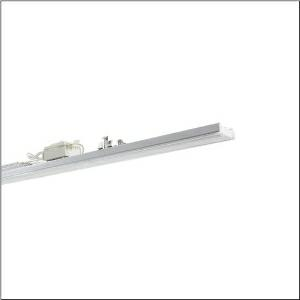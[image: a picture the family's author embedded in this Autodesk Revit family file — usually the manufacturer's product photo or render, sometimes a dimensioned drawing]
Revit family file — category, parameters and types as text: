
# Revit family: licross_r__11_recessed_ho_51tl18dv4m1m_dde3
name_source: partatom
category: Lighting Fixtures
units: mm (PartAtom-declared; Revit-internal decimal feet)

## family parameters
Cut with Voids When Loaded = No
Host = Face
Light Source = No
Part Type = Normal
Room Calculation Point = No
Round Connector Dimension = Use Diameter
Shared = No

## types (1)
- --- (1 x LED, 26860 lm, 150.5 W, 4000K)
    Apparent Load = 150 VA
    CIE Flux Codes = 78 94 99 100 100
    Color Rendering = 80
    Color Temperature = 4000K
    Default Elevation = 1800 mm
    Description = Licross® 11 Recessed HO, luminaire insert, of sheet steel, coil coated, white, length: 2.250mm, width: 66mm, height: 67mm, LED rated luminous flux: 26.870lm, light colour: 840, control gear: DALI 2, with plug, 5-pole, with phase selection, mains connection: 220..240V, AC, 50/60Hz, rated input power: 151W, halogen-free wiring, primary light control with lens, of plastic, primary optical cover: cover, of PMMA, light emission: direct distribution, primary light characteristic: symmetric, protection rating (complete): IP40, insulation class (complete): insulation class I (protective earthing), certification: CE, ENEC, VDE, UKCA, protection symbol: D if used in an environment without relevant dust loads with corresponding accessories, impact resistance: IK06, permissible ambient temperature for indoor applications: -40..+35°C, corresponds to IFS (International Featured Standards) requirements for safety and quality in the food industry, reducing of maximum allowable ambient temperature of 5°C with ceiling mounting, LABS conformity tested according to VDMA 24364:2018-05, packaging unit: 1 piece
    Height = 58 mm
    Lamp = 1 x LED
    Lamp Light Flux = 26860 lm
    Lamp Power = 150.5 W
    Lamp count = 1
    Length = 2250 mm
    Luminous efficacy = 178 lm/W
    Manufacturer = Siteco
    ModVariant = No
    Model = 51TL18DV4M1M
    Mounting Place = Ceiling
    Mounting Type = Pendant
    Number of Poles = 1
    OnlyDefault = Yes
    Power Factor = 1
    Product Name = Licross® 11 Recessed HO
    Product group = luminaire insert
    ProductGroupID = 902
    Protection Class = Protection class I
    Protection Degree = IP 40
    RLX_Detail_Level = 1
    RLX_Emergency_Light_Flux = 0 lm
    RLX_Emergency_Type = 0
    RLX_Emergency_Type_DB = No
    RlxData = <blob elided: 29361 chars, md5=500fe299>
    Socket = socket
    Standby Power = 0 W
    System Light Flux = 26860 lm
    System Power = 150 W
    Type Comments = factory setting: luminous flux: 100 % | dim-lin: 254 | 690 mA
    Type Image = l_1296930.jpg
    URL = http://relux.com
    VarID = @adj_099446
    Voltage = 0 V
    Weight = 0.00 kg
    Width = 66 mm

## geometry (parser evidence)
native form markers: Blend x4, Sweep x9
no freeform markers — native parametric forms only
